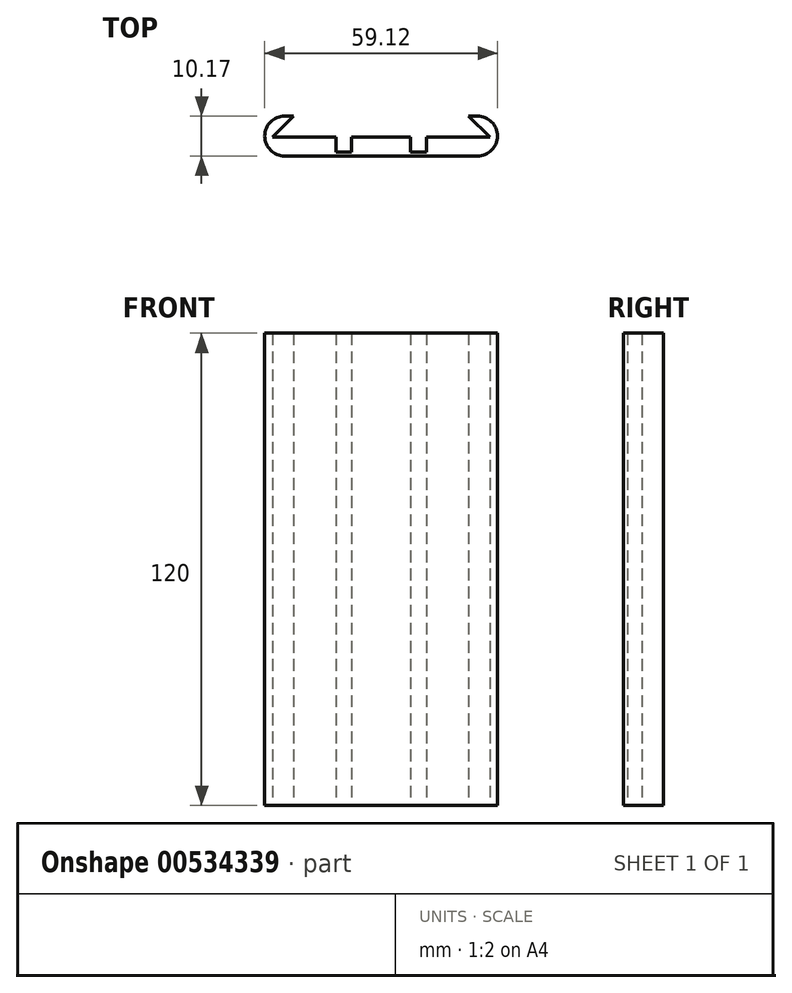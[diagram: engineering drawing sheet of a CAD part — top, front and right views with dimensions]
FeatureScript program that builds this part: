
annotation { "Feature Type Name" : "Feature", "Feature Type Description" : "" }
export const myFeature = defineFeature(function(context is Context, id is Id, definition is map)
    precondition{}
    {
        {
            var Q0;
            Q0=qCreatedBy(makeId("Top.planeOp"),FACE);
            var sketch = newSketch(context, id + "F0", { "sketchPlane" : qUnion([Q0])});
            skLineSegment(sketch, "E0.top", {"start": v(29.56, -7.15) * mm, "end": v(-29.56, -7.15) * mm});
            skLineSegment(sketch, "E0.left", {"start": v(29.56, 3.02) * mm, "end": v(29.56, -7.15) * mm});
            skLineSegment(sketch, "E0.right", {"start": v(-29.56, 3.02) * mm, "end": v(-29.56, -7.15) * mm});
            skPoint(sketch, "E0.middle", {"position": v(0, 0) * mm});
            skPoint(sketch, "E1", {"position": v(-17.65, 7.62) * mm});
            skPoint(sketch, "E2", {"position": v(17.65, 7.62) * mm});
            skLineSegment(sketch, "E3.top", {"start": v(-27.65, -2.38) * mm, "end": v(-11.5, -2.38) * mm});
            skLineSegment(sketch, "E3.left", {"start": v(-22.24, 3.02) * mm, "end": v(-27.65, -2.38) * mm});
            skLineSegment(sketch, "E3.right", {"start": v(22.24, 3.02) * mm, "end": v(27.65, -2.38) * mm});
            skLineSegment(sketch, "E4", {"start": v(-7.5, -2.38) * mm, "end": v(-7.5, -6.15) * mm});
            skLineSegment(sketch, "E5", {"start": v(7.5, -2.38) * mm, "end": v(7.5, -6.15) * mm});
            skPoint(sketch, "E6", {"position": v(0, -2.38) * mm});
            skLineSegment(sketch, "E7", {"start": v(0, -2.38) * mm, "end": v(0, -7.15) * mm, "construction": true});
            skLineSegment(sketch, "E8", {"start": v(-11.5, -2.38) * mm, "end": v(-11.5, -6.15) * mm});
            skLineSegment(sketch, "E9", {"start": v(11.5, -2.38) * mm, "end": v(11.5, -6.15) * mm});
            skLineSegment(sketch, "E10", {"start": v(-11.5, -4.77) * mm, "end": v(-7.5, -4.77) * mm, "construction": true});
            skLineSegment(sketch, "E11", {"start": v(7.5, -4.77) * mm, "end": v(11.5, -4.77) * mm, "construction": true});
            skLineSegment(sketch, "E12", {"start": v(-11.5, -6.15) * mm, "end": v(-7.5, -6.15) * mm});
            skLineSegment(sketch, "E13", {"start": v(-3.71, -6.15) * mm, "end": v(-3.71, -7.15) * mm, "construction": true});
            skLineSegment(sketch, "E14.trimOffspring", {"start": v(7.5, -6.15) * mm, "end": v(11.5, -6.15) * mm});
            skPoint(sketch, "E15.orphan", {"position": v(-11.5, -7.15) * mm});
            skPoint(sketch, "E16.orphan", {"position": v(-7.5, -7.15) * mm});
            skPoint(sketch, "E17.orphan", {"position": v(7.5, -7.15) * mm});
            skPoint(sketch, "E18.orphan", {"position": v(11.5, -7.15) * mm});
            skLineSegment(sketch, "E19.trimOffspring", {"start": v(11.5, -2.38) * mm, "end": v(27.65, -2.38) * mm});
            skLineSegment(sketch, "E20.trimOffspring", {"start": v(-7.5, -2.38) * mm, "end": v(7.5, -2.38) * mm});
            skPoint(sketch, "E21.start.orphan", {"position": v(0, -4.77) * mm});
            skLineSegment(sketch, "E22", {"start": v(-29.56, 3.02) * mm, "end": v(-22.24, 3.02) * mm});
            skLineSegment(sketch, "E23.trimOffspring", {"start": v(22.24, 3.02) * mm, "end": v(29.56, 3.02) * mm});
            skPoint(sketch, "E24.trimOffspring.end.orphan", {"position": v(-29.56, 7.15) * mm});
            skPoint(sketch, "E25.orphan", {"position": v(29.56, 7.15) * mm});
            skLineSegment(sketch, "E26", {"start": v(-27.65, -2.38) * mm, "end": v(27.65, -2.38) * mm, "construction": true});
            skLineSegment(sketch, "E27", {"start": v(-7.5, -3.85) * mm, "end": v(0, -3.85) * mm, "construction": true});
            skLineSegment(sketch, "E28", {"start": v(0, -3.85) * mm, "end": v(7.5, -3.85) * mm, "construction": true});
            skSolve(sketch);
        }
        {
            var Q0;
            Q0 = qSketchRegion(id + "F0", true);
            extrude(context, id + "F1", {"entities" : qUnion([Q0]), "depth" : 120 * mm, "offsetDistance" : 25.4 * mm});
        }
        {
            var Q0;
            Q0=makeQuery(id+"F1.opExtrude","SWEPT_EDGE",EDGE,{"disambiguationData":[OSD([sQuery(id+"F0.wireOp",EDGE,"E0.right"),sQuery(id+"F0.wireOp",EDGE,"E22")])]});
            var Q1;
            Q1=makeQuery(id+"F1.opExtrude","SWEPT_EDGE",EDGE,{"disambiguationData":[OSD([sQuery(id+"F0.wireOp",EDGE,"E0.top"),sQuery(id+"F0.wireOp",EDGE,"E0.right")])]});
            var Q2;
            Q2=makeQuery(id+"F1.opExtrude","SWEPT_EDGE",EDGE,{"disambiguationData":[OSD([sQuery(id+"F0.wireOp",EDGE,"E0.top"),sQuery(id+"F0.wireOp",EDGE,"E0.left")])]});
            var Q3;
            Q3=makeQuery(id+"F1.opExtrude","SWEPT_EDGE",EDGE,{"disambiguationData":[OSD([sQuery(id+"F0.wireOp",EDGE,"E0.left"),sQuery(id+"F0.wireOp",EDGE,"E23.trimOffspring")])]});
            fillet(context, id + "F2", {"entities" : qUnion([Q0, Q1, Q2, Q3]), "radius" : 5.08 * mm, "tangentPropagation" : true, "allowEdgeOverflow" : false});
        }
    });
